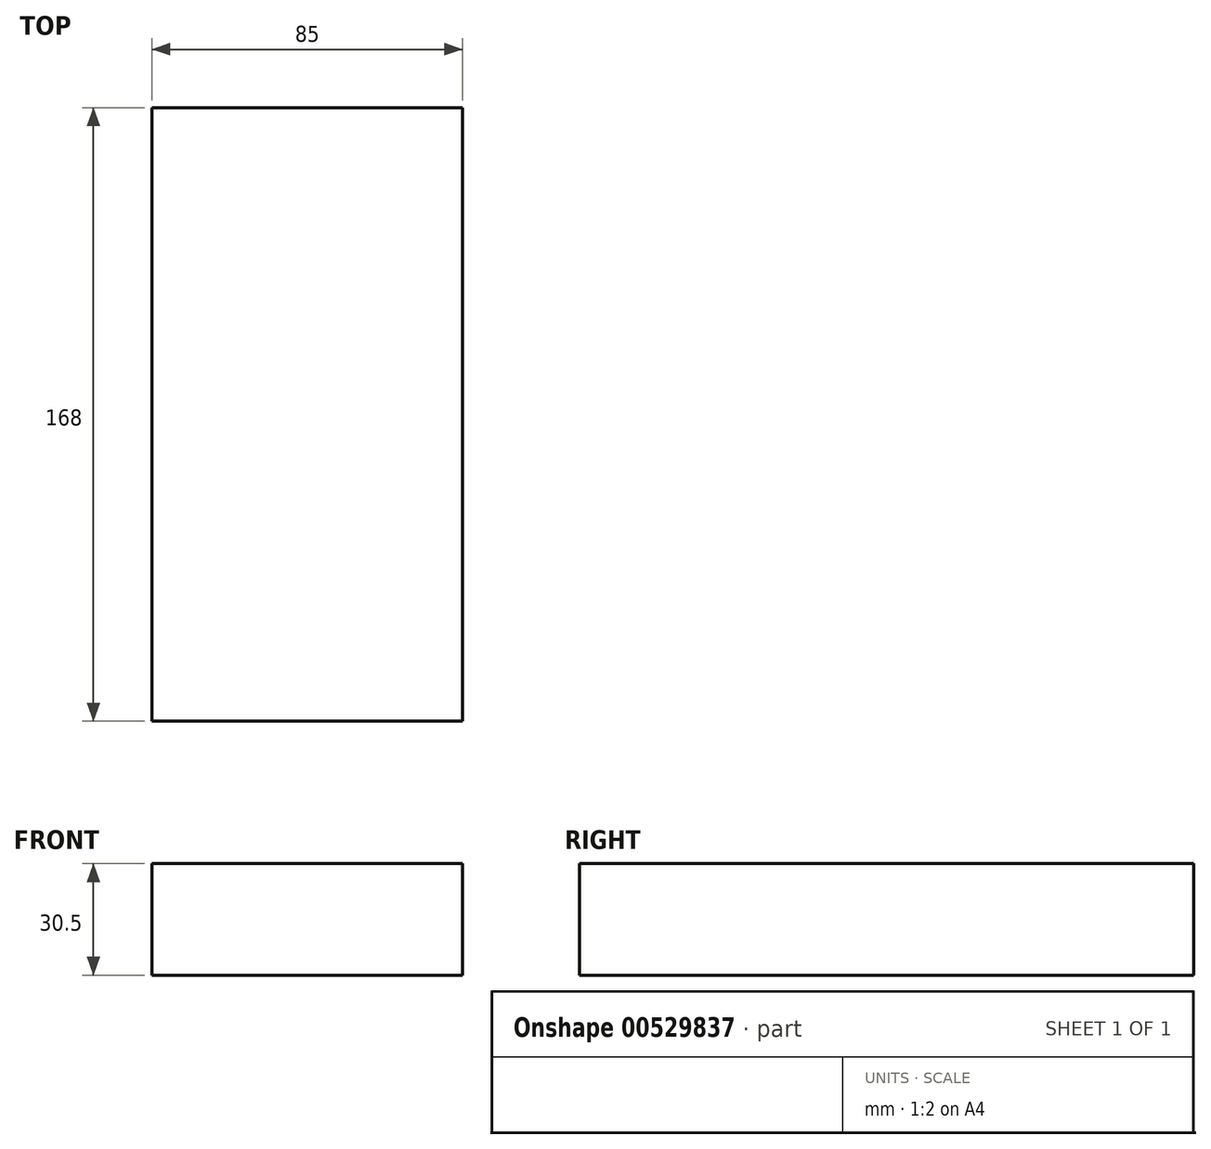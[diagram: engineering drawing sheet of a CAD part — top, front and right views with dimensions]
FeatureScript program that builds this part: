
annotation { "Feature Type Name" : "Feature", "Feature Type Description" : "" }
export const myFeature = defineFeature(function(context is Context, id is Id, definition is map)
    precondition{}
    {
        {
            assignVariable(context, id + "F0", {"name" : "MedalBoxThickness", "anyValue" : 30.5});
        }
        {
            var Q0;
            Q0=qCreatedBy(makeId("Top.planeOp"),FACE);
            var sketch = newSketch(context, id + "F1", { "sketchPlane" : qUnion([Q0])});
            skLineSegment(sketch, "E0.bottom", {"start": v(42.5, -84) * mm, "end": v(-42.5, -84) * mm});
            skLineSegment(sketch, "E0.top", {"start": v(42.5, 84) * mm, "end": v(-42.5, 84) * mm});
            skLineSegment(sketch, "E0.left", {"start": v(42.5, -84) * mm, "end": v(42.5, 84) * mm});
            skLineSegment(sketch, "E0.right", {"start": v(-42.5, -84) * mm, "end": v(-42.5, 84) * mm});
            skPoint(sketch, "E0.middle", {"position": v(0, 0) * mm});
            skSolve(sketch);
        }
        {
            var Q0;
            Q0 = qSketchRegion(id + "F1", true);
            extrude(context, id + "F2", {"entities" : qUnion([Q0]), "depth" : (getVariable(context, 'MedalBoxThickness')) * mm, "offsetDistance" : 25 * mm});
        }
    });
